# Revit family: WL118-sw
name_source: partatom
category: Communication Devices
revit_build: Autodesk Revit Architecture 2012 (Build: 20110309_2315(x64)
units: mm (PartAtom-declared; Revit-internal decimal feet)

## types (1)
- WL118-sw
    Default Elevation = 48"
    Depth = 30.375"
    Description = Vented 18" Subwoofer
    Enclosure Material = Black Finish
    Enclosure with Rig Bar Width = 27"
    Front Handle Offset = 7.678"
    Front Rig Bar Center Offset = 1.866"
    Grill Depth = 2.05"
    Grill Width = 24.484"
    Grille Material = Black Grille
    Height = 22.1"
    Impedance = 8
    Inner Enclosure Height = 20.1"
    Inner Enclosure Width = 25.8"
    Manufacturer = QSC Audio Products, LLC
    Manufacturer URL = www.qscaudio.com
    Model = WL118-sw
    Overall Depth = 30.375"
    Overall Height = 22.1"
    Overall Width = 27.6"
    Power Handling = 1750
    Product Documentation Link = http://media.qscaudio.com
    Product Page URL = http://www.qscaudio.com
    Rear Handle Offset = 23.603"
    Rear Rig Bar Center Offset = 12.616"
    Regulatory Compliance = RoHS
    SPL Max = 128.5
    Sensitivity = 98
    URL = http://www.qscaudio.com
    Weight Dimensional (kg) = 55
    Weight Dimensional (lb) = 121
    Weight Product (kg) = 50.4
    Weight Product (lb) = 111
    Width = 27.6"

## geometry (parser evidence)
native form markers: Sweep x1
no freeform markers — native parametric forms only
